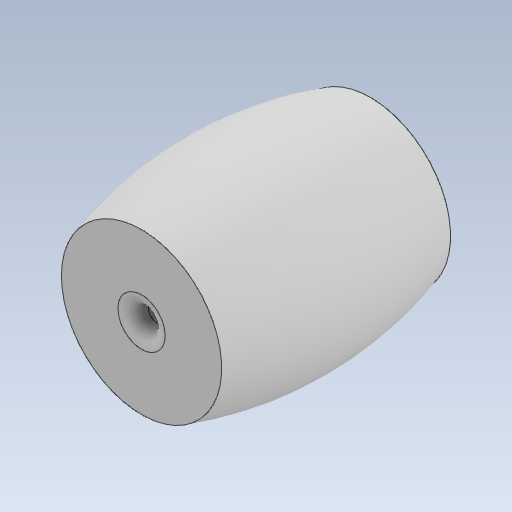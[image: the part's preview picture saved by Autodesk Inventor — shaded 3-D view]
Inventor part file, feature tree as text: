
AUTODESK INVENTOR PART (.ipt)
format: ipt  version: 2021 (Build 250183000, 183)  size: 135,168 bytes
history: native  units: in
note: dims shown in document units (in); Inventor stores cm internally (conversion verified against a paired STEP export)
features: revolve x1, fillet x1, sketch x1
ambient origin geometry x8: Origin, YZ Plane, XZ Plane, XY Plane, X Axis, Y Axis, Z Axis, Center Point
bodies: Solid1 (feature_tree)
feature tree (3):
  revolve  "Revolution1"  [1 undecoded]
  fillet  "Fillet1"  Radius=0.9843in
  sketch  "Sketch1"  dims[d0=0.5906in d1=0.2067in d2=0.9843in d3=0.0217in d4=90.0deg d5=0.0394in]
note: 1 required parameter value undecoded (feature->parameter linkage not recoverable at this tier; creation-order binding heuristic only, values carry confidence <= 0.55)
